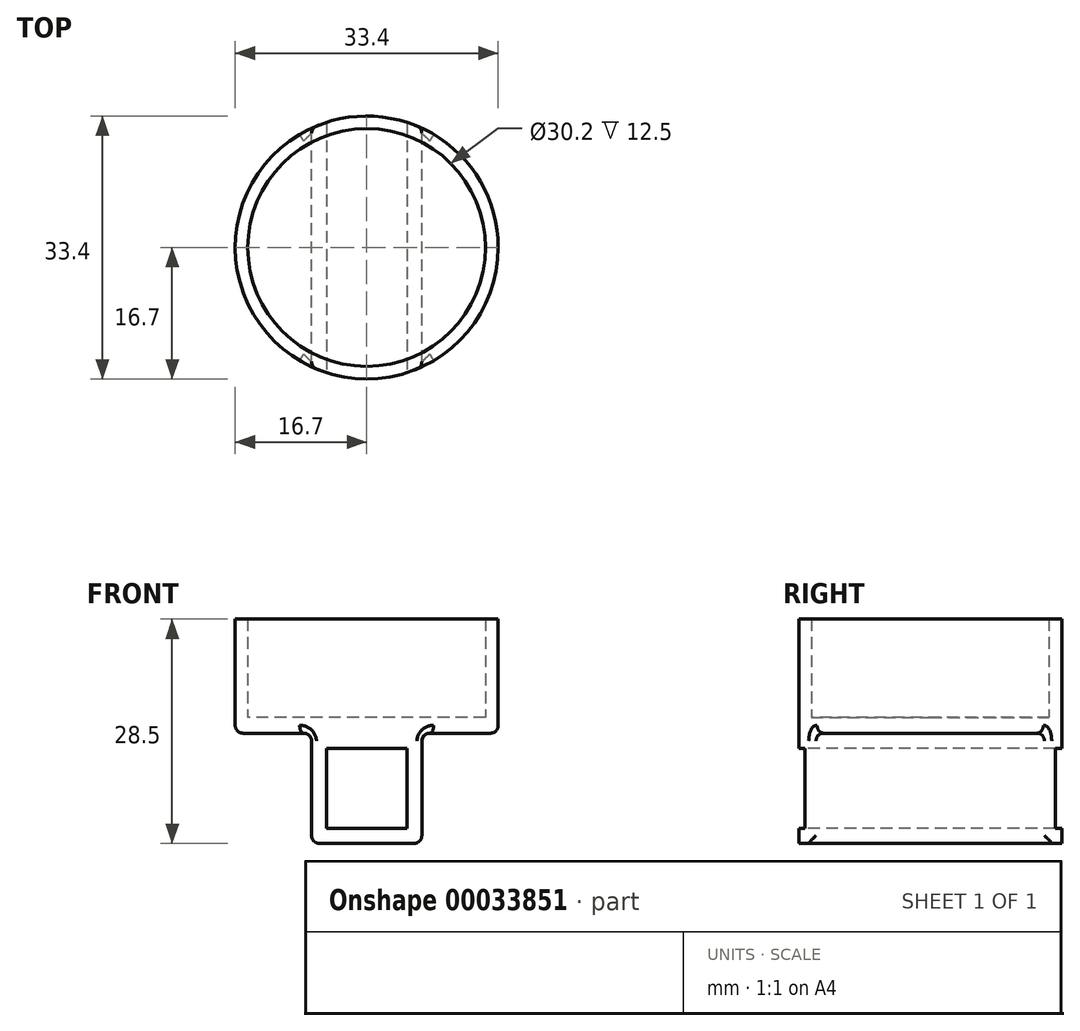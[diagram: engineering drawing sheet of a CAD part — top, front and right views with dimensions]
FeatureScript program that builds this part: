
annotation { "Feature Type Name" : "Feature", "Feature Type Description" : "" }
export const myFeature = defineFeature(function(context is Context, id is Id, definition is map)
    precondition{}
    {
        {
            var Q0;
            Q0=qCreatedBy(makeId("Top.planeOp"),FACE);
            var sketch = newSketch(context, id + "F0", { "sketchPlane" : qUnion([Q0])});
            skCircle(sketch, "E0", {"center": v(0, 0) * mm, "radius": 15.1 * mm});
            skCircle(sketch, "E1.0", {"center": v(0, 0) * mm, "radius": 16.7 * mm});
            skSolve(sketch);
        }
        {
            var Q0;
            Q0=qSketchRegion(id+"F0",true);
            extrude(context, id + "F1", {"entities" : qUnion([Q0]), "depth" : 12.5 * mm});
        }
        {
            var Q0;
            Q0=qCreatedBy(makeId("Top.planeOp"),FACE);
            var sketch = newSketch(context, id + "F2", { "sketchPlane" : qUnion([Q0])});
            skCircle(sketch, "E2", {"center": v(0, 0) * mm, "radius": 16.7 * mm});
            skSolve(sketch);
        }
        {
            var Q0;
            Q0=qSketchRegion(id+"F2",true);
            extrude(context, id + "F3", {"entities" : qUnion([Q0]), "operationType" : NewBodyOperationType.ADD, "oppositeDirection" : true, "depth" : 2 * mm});
        }
        {
            var Q0;
            Q0=makeQuery(id+"F3.opExtrude","CAP_FACE",FACE,{"disambiguationData":[OSD([sQuery(id+"F2.wireOp",EDGE,"E2")])],"isStart":false});
            var sketch = newSketch(context, id + "F4", { "sketchPlane" : qUnion([Q0])});
            skLineSegment(sketch, "E3.rect.left", {"start": v(7, 15.16) * mm, "end": v(7, -15.16) * mm});
            skLineSegment(sketch, "E3.rect.right", {"start": v(-7, 15.16) * mm, "end": v(-7, -15.16) * mm});
            skPoint(sketch, "E3.rect.middle", {"position": v(0, 0) * mm});
            skArc(sketch, "E4", {"start": v(7, 15.16) * mm, "mid": v(0, 16.7) * mm, "end": v(-7, 15.16) * mm});
            skArc(sketch, "E5.MirrorCS", {"start": v(7, -15.16) * mm, "mid": v(0, -16.7) * mm, "end": v(-7, -15.16) * mm});
            skSolve(sketch);
        }
        {
            var Q0;
            Q0=qSketchRegion(id+"F4",true);
            extrude(context, id + "F5", {"entities" : qUnion([Q0]), "operationType" : NewBodyOperationType.ADD, "depth" : 14 * mm});
        }
        {
            var Q0;
            Q0=qCreatedBy(makeId("Front.planeOp"),FACE);
            var sketch = newSketch(context, id + "F6", { "sketchPlane" : qUnion([Q0])});
            skLineSegment(sketch, "E6.0", {"start": v(-5.1, -14.1) * mm, "end": v(-5.1, -3.9) * mm});
            skLineSegment(sketch, "E6.1", {"start": v(-5.1, -14.1) * mm, "end": v(5.1, -14.1) * mm});
            skLineSegment(sketch, "E6.2", {"start": v(5.1, -14.1) * mm, "end": v(5.1, -3.9) * mm});
            skLineSegment(sketch, "E7", {"start": v(-5.1, -3.9) * mm, "end": v(5.1, -3.9) * mm});
            skSolve(sketch);
        }
        {
            var Q0;
            Q0=qSketchRegion(id+"F6",true);
            extrude(context, id + "F7", {"entities" : qUnion([Q0]), "operationType" : NewBodyOperationType.REMOVE, "endBound" : BoundingType.SYMMETRIC, "oppositeDirection" : true, "depth" : 50 * mm});
        }
        {
            var Q0;
            {var subQ0=sQuery(id+"F2.wireOp",EDGE,"E2");Q0=makeQuery(id+"F5.boolean.opBoolean","SPLIT",EDGE,{"disambiguationData":[TD([makeQuery(id+"F5.opExtrude","SWEPT_FACE",FACE,{"disambiguationData":[OSD([sQuery(id+"F4.wireOp",EDGE,"E3.rect.left")])]})])],"derivedFrom":makeQuery(id+"F3.opExtrude","CAP_EDGE",EDGE,{"disambiguationData":[OSD([subQ0])],"isStart":false})});}
            var Q1;
            {var subQ0=sQuery(id+"F2.wireOp",EDGE,"E2");Q1=makeQuery(id+"F5.boolean.opBoolean","SPLIT",EDGE,{"disambiguationData":[TD([makeQuery(id+"F5.opExtrude","SWEPT_FACE",FACE,{"disambiguationData":[OSD([sQuery(id+"F4.wireOp",EDGE,"E3.rect.right")])]})])],"derivedFrom":makeQuery(id+"F3.opExtrude","CAP_EDGE",EDGE,{"disambiguationData":[OSD([subQ0])],"isStart":false})});}
            var Q2;
            Q2=makeQuery(id+"F5.opExtrude","SWEPT_FACE",FACE,{"disambiguationData":[OSD([sQuery(id+"F4.wireOp",EDGE,"E3.rect.left")])]});
            var Q3;
            Q3=makeQuery(id+"F5.opExtrude","SWEPT_FACE",FACE,{"disambiguationData":[OSD([sQuery(id+"F4.wireOp",EDGE,"E3.rect.right")])]});
            fillet(context, id + "F8", {"entities" : qUnion([Q0, Q1, Q2, Q3]), "radius" : 1 * mm, "tangentPropagation" : true, "allowEdgeOverflow" : false});
        }
    });
